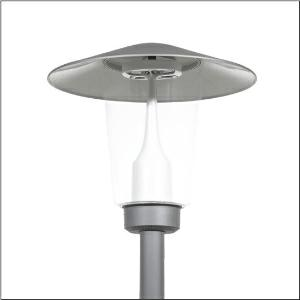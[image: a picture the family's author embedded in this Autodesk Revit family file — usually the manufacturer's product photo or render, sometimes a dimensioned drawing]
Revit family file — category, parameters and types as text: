
# Revit family: pilzleuchte_iq___st1_2a_5xa5235ef14h_b780
name_source: partatom
category: Lighting Fixtures
units: mm (PartAtom-declared; Revit-internal decimal feet)

## family parameters
Cut with Voids When Loaded = No
Host = Face
Light Source = No
Part Type = Normal
Room Calculation Point = No
Round Connector Dimension = Use Diameter
Shared = No

## types (1)
- --- (1 x LED, 1550 lm, 10.5 W, 3000K)
    Apparent Load = 11 VA
    CIE Flux Codes = 24 61 93 98 100
    Color Rendering = 70
    Color Temperature = 3000K
    Default Elevation = 1800 mm
    Description = Mushroom Luminaire iQ, mast luminaire, Module 540 iQ-SR, primary light control with 3 zone facetted reflector, of plastic, silver coated, highly specular, structured, primary optical cover: cover, of PMMA, transparent, light distribution: ST1.2a, light emission: direct distribution, primary light characteristic: asymmetric, installation type: post-top, LED, High Power LED, rated luminous flux: 1.550lm, luminous efficacy: 148lm/W, light colour: 730, colour temperature: 3000K, control gear: ECG iQ, control: Auto-Match, Temp-Guard, Lumen-Switch, Night-Set, Smart-Wire, Light-Fading, Desk-Remote (wireless, voltage-free reading and setting of iQ features in the workshop via application-optimized NFC function/RFID function), optimised constant luminous flux control (CLO 2.0), Street-Remote, presetting dimming logarithmic, with terminal, 6-pole, max. 2.5mm², mains connection: 230..240V, AC, 50/60Hz, start of lifetime: 11W, end of service life: 11W, reduction: 5W, luminaire housing, upper part, of glass-fibre reinforced polyester, coated, Siteco® metallic grey (DB 702S), diameter: 650mm, height: 586mm, spigot size: d x l = 76 x 70mm (post-top) | with reducer (optional accessory) 60 x 70mm, post-top mast mounting element, of diecast aluminium, coated, Siteco® metallic grey (DB 702S), Module 540 iQ-SR, traffic white (RAL 9016), equipment: standard, protection rating (complete): IP65, insulation class (complete): insulation class II (safety insulation), certification: CE, ENEC, VDE, packaging unit: 1 piece

Light Distribution: ST1.2a
    Height = 586 mm
    Lamp = 1 x LED
    Lamp Light Flux = 1550 lm
    Lamp Power = 10.5 W
    Lamp count = 1
    Length = 650 mm
    Luminous efficacy = 148 lm/W
    Manufacturer = Siteco
    ModVariant = No
    Model = 5XA5235EF14H
    Number of Poles = 1
    OnlyDefault = Yes
    Power Factor = 1
    Product Name = Pilzleuchte iQ | ST1.2a
    Product group = mast luminaire | pylon top
    ProductGroupID = 6100
    Protection Class = Protection class II
    Protection Degree = IP 65
    RLX_Detail_Level = 1
    RLX_Emergency_Light_Flux = 0 lm
    RLX_Emergency_Type = 0
    RLX_Emergency_Type_DB = No
    RlxData = <blob elided: 123041 chars, md5=454c7a0d>
    Socket = socket
    Standby Power = 0 W
    System Light Flux = 1550 lm
    System Power = 11 W
    Type Comments = factory setting: luminous flux: 100 % | dim-lin: 254 | 419 mA
    Type Image = l_1006077.jpg
    URL = http://relux.com
    VarID = @adj_110941
    Voltage = 0 V
    Weight = 0.00 kg
    Width = 0 mm  [stored 0 ft]

note: [stored X ft] marks values corroborated as IEEE doubles in the binary element streams (Revit-internal decimal feet)

## geometry (parser evidence)
native form markers: Blend x4, Sweep x14
no freeform markers — native parametric forms only
